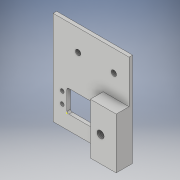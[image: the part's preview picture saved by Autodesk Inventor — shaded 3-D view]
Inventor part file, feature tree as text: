
AUTODESK INVENTOR PART (.ipt)
format: ipt  version: 2017 (Build 210142000, 142)  size: 267,264 bytes
history: native  units: in
note: dims shown in document units (in); Inventor stores cm internally (conversion verified against a paired STEP export)
features: sketch x14, extrude x12, thread x7, fillet x4, projected_geometry x3, hole x1
ambient origin geometry x8: Origin, YZ Plane, XZ Plane, XY Plane, X Axis, Y Axis, Z Axis, Center Point
bodies: Solid1 (feature_tree)
feature tree (41):
  extrude  "Extrusion1"  Depth=0.78in
  extrude  "Extrusion2"  Depth=0.125in
  extrude  "Extrusion3"  Depth=0.125in
  extrude  "Extrusion4"  Depth=0.135in
  extrude  "Extrusion7"  Depth=0.125in TaperAngle=0.0deg
  sketch  "Sketch9"  dims[d21=0.125in d22=0.324in d23=0.0in d33=0.75in d34=0.324in d35=0.0in d36=1.78in d41=0.25in]
  extrude  "Extrusion9"  Depth=0.324in TaperAngle=0.0deg
  thread  "Thread1"  [1 undecoded]
  thread  "Thread2"  [1 undecoded]
  thread  "Thread3"  [1 undecoded]
  thread  "Thread4"  [1 undecoded]
  extrude  "Extrusion10"  Depth=0.2in
  hole  "Hole1"  [1 undecoded]
  extrude  "Extrusion11"  Depth=1.0in TaperAngle=0.0deg
  sketch  "Sketch14"  dims[d58=0.356in d59=0.25in]
  extrude  "Extrusion12"  Depth=0.125in TaperAngle=0.0deg
  extrude  "Extrusion15"  Depth=0.25in
  thread  "Thread5"  [1 undecoded]
  thread  "Thread6"  [1 undecoded]
  sketch  "Sketch18"  dims[d74=0.45in d75=0.45in d82=0.19in d83=0.19in d84=1.0in d85=0.0in d86=1.0in d87=0.0in d88=1.0in d89=0.0in d90=0.38in d91=0.25in d92=0.0in d93=1.0in d94=0.0in d95=1.78in d96=2.528in d98=0.5in d99=0.25in d100=0.0in d101=0.06in d102=0.06in d103=0.06in d104=0.06in d106=0.484in d107=0.165in d108=1.56in d109=0.693in d110=1.087in d111=0.165in d112=0.165in d113=0.165in]
  extrude  "Extrusion16"  Depth=0.874in
  thread  "Thread7"  [1 undecoded]
  extrude  "Extrusion17"  Depth=1.56in
  fillet  "Fillet1"  Radius=0.19in
  fillet  "Fillet2"  Radius=0.19in
  fillet  "Fillet3"  Radius=1.0in
  fillet  "Fillet4"  Radius=1.0in
  sketch  "Sketch1"  dims[d0=1.56in d1=0.78in]
  sketch  "Sketch2"  dims[d6=0.125in d7=0.0in d10=0.083in]
  sketch  "Sketch3"  dims[d11=0.125in d12=0.0in d15=0.135in]
  sketch  "Sketch4"  dims[d16=0.135in d17=0.135in]
  sketch  "Sketch8"  dims[d18=0.135in d19=0.125in d20=0.0in]
  sketch  "Sketch10"  dims[d44=0.2in d45=0.0in d46=1.89in]
  sketch  "Sketch11"  dims[d47=1.89in d48=1.0in d49=0.0in]
  sketch  "Sketch12"  dims[d50=1.0in d51=0.0in d52=1.0in d53=0.0in]
  projected_geometry  "Projected Loop1"
  projected_geometry  "Projected Loop2"
  projected_geometry  "Projected Loop3"
  sketch  "Sketch13"  dims[d54=1.0in d55=0.0in d56=0.125in d57=0.0in]
  sketch  "Sketch15"  dims[d60=0.25in d61=0.75in d62=0.375in d63=0.25in d64=0.5635in d65=0.25in d66=0.0in d67=0.01in d68=0.0in d69=1.5in d70=0.0in]
  sketch  "Sketch16"  dims[d71=0.75in d72=0.874in d73=0.53in]
note: 8 required parameter values undecoded (feature->parameter linkage not recoverable at this tier; creation-order binding heuristic only, values carry confidence <= 0.55)
